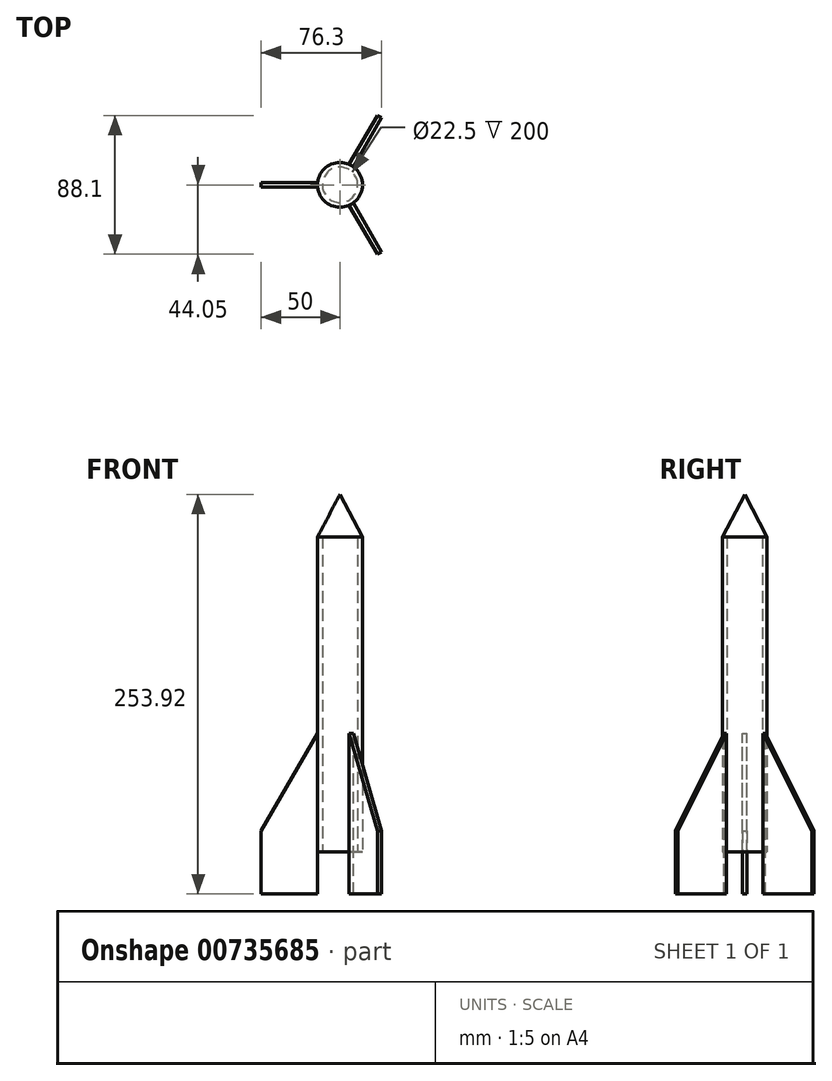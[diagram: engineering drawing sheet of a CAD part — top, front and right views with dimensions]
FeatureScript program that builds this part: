
annotation { "Feature Type Name" : "Feature", "Feature Type Description" : "" }
export const myFeature = defineFeature(function(context is Context, id is Id, definition is map)
    precondition{}
    {
        {
            var Q0;
            Q0=qCreatedBy(makeId("Front.planeOp"),FACE);
            var sketch = newSketch(context, id + "F0", { "sketchPlane" : qUnion([Q0])});
            skLineSegment(sketch, "E0", {"start": v(0, 0) * mm, "end": v(0, 227) * mm, "construction": true});
            skLineSegment(sketch, "E1", {"start": v(0, 227) * mm, "end": v(-14.25, 200) * mm});
            skLineSegment(sketch, "E2", {"start": v(-14.25, 200) * mm, "end": v(-14.25, 0) * mm});
            skLineSegment(sketch, "E3", {"start": v(-14.25, 0) * mm, "end": v(-11.25, 0) * mm});
            skLineSegment(sketch, "E4", {"start": v(-11.25, 0) * mm, "end": v(-11.25, 200) * mm});
            skLineSegment(sketch, "E5", {"start": v(-11.25, 200) * mm, "end": v(0, 200) * mm});
            skLineSegment(sketch, "E6", {"start": v(0, 227) * mm, "end": v(0, 200) * mm});
            skSolve(sketch);
        }
        {
            var Q0;
            Q0=qSketchRegion(id+"F0",true);
            var Q1;
            Q1=sQuery(id+"F0.wireOp",EDGE,"E0");
            revolve(context, id + "F1", {"surfaceOperationType" : NewSurfaceOperationType.NEW, "entities" : qUnion([Q0]), "axis" : qUnion([Q1]), "revolveType" : RevolveType.FULL});
        }
        {
            var Q0;
            Q0=qCreatedBy(makeId("Front.planeOp"),FACE);
            var sketch = newSketch(context, id + "F2", { "sketchPlane" : qUnion([Q0])});
            skLineSegment(sketch, "E7", {"start": v(-50, 13.08) * mm, "end": v(-14.25, 75) * mm});
            skLineSegment(sketch, "E8", {"start": v(-14.25, -26.92) * mm, "end": v(-50, -26.92) * mm});
            skLineSegment(sketch, "E9", {"start": v(-50, 13.08) * mm, "end": v(-50, -26.92) * mm});
            skLineSegment(sketch, "E10", {"start": v(-14.25, -16.92) * mm, "end": v(-14.25, 200) * mm});
            skLineSegment(sketch, "E11", {"start": v(14.25, 200) * mm, "end": v(14.25, 0) * mm});
            skLineSegment(sketch, "E12", {"start": v(-14.25, -16.92) * mm, "end": v(-14.25, -26.92) * mm});
            skLineSegment(sketch, "E13", {"start": v(-14.25, 0) * mm, "end": v(-14.25, 200) * mm});
            skLineSegment(sketch, "E14.0", {"start": v(14.25, 200) * mm, "end": v(-14.25, 200) * mm});
            skSolve(sketch);
        }
        {
            var Q0;
            Q0=qSketchRegion(id+"F2",true);
            extrude(context, id + "F3", {"entities" : qUnion([Q0]), "operationType" : NewBodyOperationType.ADD, "endBound" : BoundingType.SYMMETRIC, "depth" : 3 * mm, "offsetDistance" : 25 * mm});
        }
        {
            var Q0;
            Q0=makeQuery(id+"F3.opExtrude","SWEPT_BODY",BODY,{"disambiguationData":[OSD([sQuery(id+"F2.wireOp",EDGE,"E7"),sQuery(id+"F2.wireOp",EDGE,"E8"),sQuery(id+"F2.wireOp",EDGE,"E9"),sQuery(id+"F2.wireOp",EDGE,"E10"),sQuery(id+"F2.wireOp",EDGE,"E12"),sQuery(id+"F2.wireOp",EDGE,"E13")])]});
            var Q1;
            Q1=makeQuery(id+"F1.opRevolve","SWEPT_FACE",FACE,{"disambiguationData":[OSD([sQuery(id+"F0.wireOp",EDGE,"E2")])]});
            circularPattern(context, id + "F4", {"entities" : qUnion([Q0]), "axis" : qUnion([Q1]), "angle" : 360 * degree, "instanceCount" : 3, "equalSpace" : true});
        }
    });
